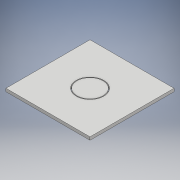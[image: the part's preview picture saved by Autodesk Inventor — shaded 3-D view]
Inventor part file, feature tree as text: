
AUTODESK INVENTOR PART (.ipt)
format: ipt  version: 2018 (Build 220112000, 112)  size: 102,400 bytes
history: native  units: mm
features: other x1, extrude x1, sketch x1
ambient origin geometry x8: Origin, YZ Plane, XZ Plane, XY Plane, X Axis, Y Axis, Z Axis, Center Point
bodies: Body1 (feature_tree)
feature tree (3):
  other  "Bryła1"
  extrude  "Wyciągnięcie proste1"  Depth=168.0mm
  sketch  "Szkic1"
